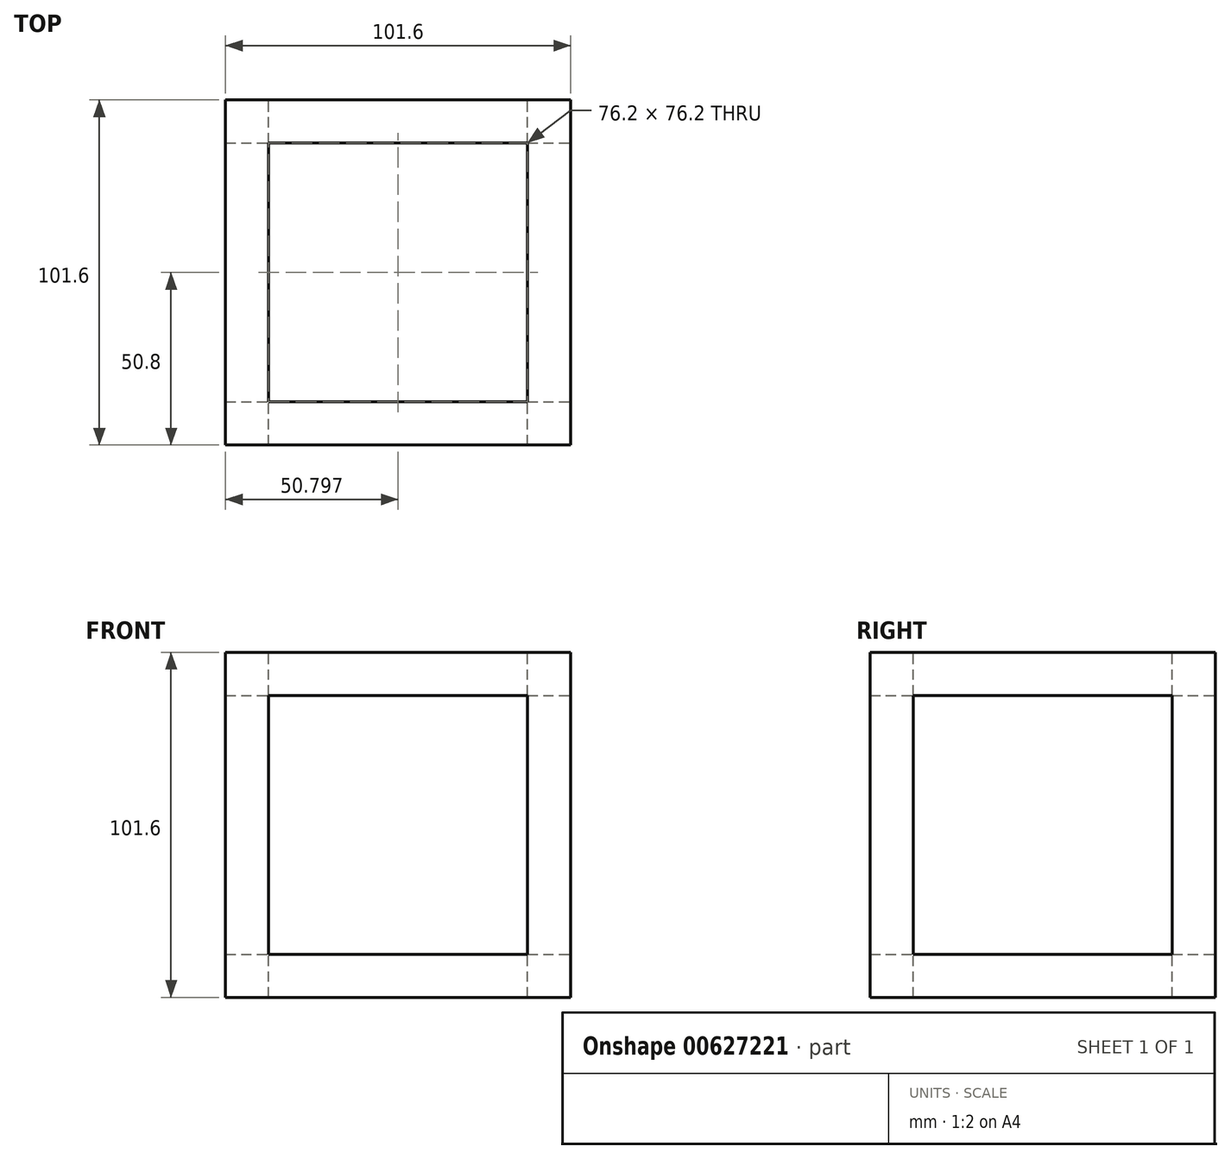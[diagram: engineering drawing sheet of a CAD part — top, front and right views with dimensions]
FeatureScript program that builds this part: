
annotation { "Feature Type Name" : "Feature", "Feature Type Description" : "" }
export const myFeature = defineFeature(function(context is Context, id is Id, definition is map)
    precondition{}
    {
        {
            var Q0;
            Q0=qCreatedBy(makeId("Front.planeOp"),FACE);
            var sketch = newSketch(context, id + "F0", { "sketchPlane" : qUnion([Q0])});
            skLineSegment(sketch, "E0", {"start": v(-55.75, 69.8) * mm, "end": v(-55.75, -31.8) * mm});
            skLineSegment(sketch, "E1", {"start": v(-55.75, -31.8) * mm, "end": v(45.85, -31.8) * mm});
            skLineSegment(sketch, "E2", {"start": v(45.85, -31.8) * mm, "end": v(45.85, 69.8) * mm});
            skLineSegment(sketch, "E3", {"start": v(45.85, 69.8) * mm, "end": v(-55.75, 69.8) * mm});
            skSolve(sketch);
        }
        {
            var Q0;
            Q0=makeQuery(id+"F0.imprint","IMPRINT",FACE,{"disambiguationData":[TD([[makeQuery(id+"F0.imprint","IMPRINT",EDGE,{"derivedFrom":sQuery(id+"F0.wireOp",EDGE,"E0")}),1.0]])]});
            extrude(context, id + "F1", {"entities" : qUnion([Q0]), "oppositeDirection" : true, "depth" : 101.6 * mm, "offsetDistance" : 25.4 * mm});
        }
        {
            var Q0;
            Q0=makeQuery(id+"F1.opExtrude","SWEPT_FACE",FACE,{"disambiguationData":[OSD([sQuery(id+"F0.wireOp",EDGE,"E3")])]});
            var sketch = newSketch(context, id + "F2", { "sketchPlane" : qUnion([Q0])});
            skLineSegment(sketch, "E4.bottom", {"start": v(-43.05, 88.9) * mm, "end": v(33.15, 88.9) * mm});
            skLineSegment(sketch, "E4.top", {"start": v(-43.05, 12.7) * mm, "end": v(33.15, 12.7) * mm});
            skLineSegment(sketch, "E4.left", {"start": v(-43.05, 88.9) * mm, "end": v(-43.05, 12.7) * mm});
            skLineSegment(sketch, "E4.right", {"start": v(33.15, 88.9) * mm, "end": v(33.15, 12.7) * mm});
            skSolve(sketch);
        }
        {
            var Q0;
            Q0=makeQuery(id+"F2.imprint","IMPRINT",FACE,{"disambiguationData":[TD([[makeQuery(id+"F2.imprint","IMPRINT",EDGE,{"derivedFrom":sQuery(id+"F2.wireOp",EDGE,"E4.bottom")}),-1.0]])]});
            extrude(context, id + "F3", {"entities" : qUnion([Q0]), "operationType" : NewBodyOperationType.REMOVE, "oppositeDirection" : true, "depth" : 76.2 * mm, "offsetDistance" : 25.4 * mm});
        }
        {
            var Q0;
            Q0=makeQuery(id+"F3.boolean.opBoolean","COPY",FACE,{"derivedFrom":makeQuery(id+"F3.opExtrude","CAP_FACE",FACE,{"disambiguationData":[OSD([sQuery(id+"F2.wireOp",EDGE,"E4.bottom"),sQuery(id+"F2.wireOp",EDGE,"E4.top"),sQuery(id+"F2.wireOp",EDGE,"E4.left"),sQuery(id+"F2.wireOp",EDGE,"E4.right")])],"isStart":false})});
            extrude(context, id + "F4", {"entities" : qUnion([Q0]), "operationType" : NewBodyOperationType.REMOVE, "oppositeDirection" : true, "depth" : 25.4 * mm, "offsetDistance" : 25.4 * mm});
        }
        {
            var Q0;
            Q0=makeQuery(id+"F1.opExtrude","CAP_FACE",FACE,{"disambiguationData":[OSD([sQuery(id+"F0.wireOp",EDGE,"E0"),sQuery(id+"F0.wireOp",EDGE,"E1"),sQuery(id+"F0.wireOp",EDGE,"E2"),sQuery(id+"F0.wireOp",EDGE,"E3")])],"isStart":false});
            var sketch = newSketch(context, id + "F5", { "sketchPlane" : qUnion([Q0])});
            skLineSegment(sketch, "E5.bottom", {"start": v(-33.15, 57.1) * mm, "end": v(43.05, 57.1) * mm});
            skLineSegment(sketch, "E5.top", {"start": v(-33.15, -19.1) * mm, "end": v(43.05, -19.1) * mm});
            skLineSegment(sketch, "E5.left", {"start": v(-33.15, 57.1) * mm, "end": v(-33.15, -19.1) * mm});
            skLineSegment(sketch, "E5.right", {"start": v(43.05, 57.1) * mm, "end": v(43.05, -19.1) * mm});
            skSolve(sketch);
        }
        {
            var Q0;
            Q0 = qSketchRegion(id + "F5", true);
            extrude(context, id + "F6", {"entities" : qUnion([Q0]), "operationType" : NewBodyOperationType.REMOVE, "oppositeDirection" : true, "depth" : 101.6 * mm, "offsetDistance" : 25.4 * mm});
        }
        {
            var Q0;
            Q0=makeQuery(id+"F1.opExtrude","SWEPT_FACE",FACE,{"disambiguationData":[OSD([sQuery(id+"F0.wireOp",EDGE,"E2")])]});
            var sketch = newSketch(context, id + "F7", { "sketchPlane" : qUnion([Q0])});
            skLineSegment(sketch, "E6.bottom", {"start": v(12.7, 57.1) * mm, "end": v(88.9, 57.1) * mm});
            skLineSegment(sketch, "E6.top", {"start": v(12.7, -19.1) * mm, "end": v(88.9, -19.1) * mm});
            skLineSegment(sketch, "E6.left", {"start": v(12.7, 57.1) * mm, "end": v(12.7, -19.1) * mm});
            skLineSegment(sketch, "E6.right", {"start": v(88.9, 57.1) * mm, "end": v(88.9, -19.1) * mm});
            skSolve(sketch);
        }
        {
            var Q0;
            Q0 = qSketchRegion(id + "F7", true);
            extrude(context, id + "F8", {"entities" : qUnion([Q0]), "operationType" : NewBodyOperationType.REMOVE, "oppositeDirection" : true, "depth" : 101.6 * mm, "offsetDistance" : 25.4 * mm});
        }
    });
